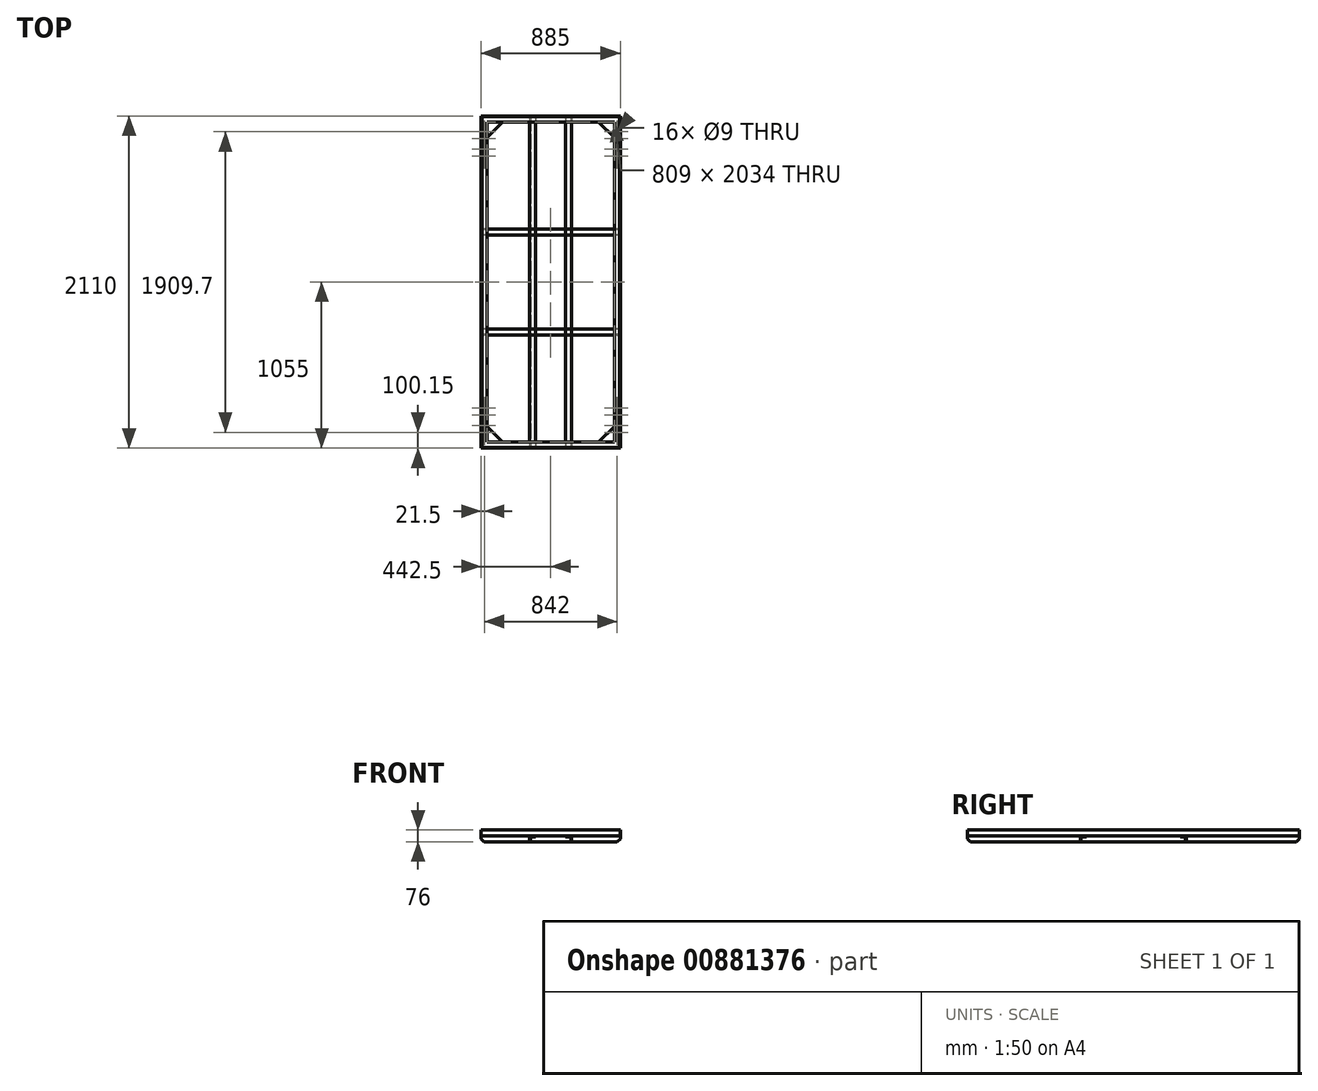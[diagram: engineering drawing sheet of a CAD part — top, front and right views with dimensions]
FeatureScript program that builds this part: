
annotation { "Feature Type Name" : "Feature", "Feature Type Description" : "" }
export const myFeature = defineFeature(function(context is Context, id is Id, definition is map)
    precondition{}
    {
        {
            var Q0;
            Q0=qCreatedBy(makeId("Top.planeOp"),FACE);
            var sketch = newSketch(context, id + "F0", { "sketchPlane" : qUnion([Q0])});
            skLineSegment(sketch, "E0.bottom", {"start": v(0, 0) * mm, "end": v(875, 0) * mm});
            skLineSegment(sketch, "E0.top", {"start": v(0, 2100) * mm, "end": v(875, 2100) * mm});
            skLineSegment(sketch, "E0.left", {"start": v(0, 0) * mm, "end": v(0, 2100) * mm});
            skLineSegment(sketch, "E0.right", {"start": v(875, 0) * mm, "end": v(875, 2100) * mm});
            skSolve(sketch);
        }
        {
            var Q0;
            Q0=qCreatedBy(makeId("Front.planeOp"),FACE);
            var sketch = newSketch(context, id + "F1", { "sketchPlane" : qUnion([Q0])});
            skLineSegment(sketch, "E1", {"start": v(0, 0) * mm, "end": v(0, 33) * mm});
            skLineSegment(sketch, "E2", {"start": v(0, 33) * mm, "end": v(-5, 33) * mm});
            skLineSegment(sketch, "E3", {"start": v(-5, 33) * mm, "end": v(-5, -5) * mm});
            skLineSegment(sketch, "E4", {"start": v(-5, -5) * mm, "end": v(33, -5) * mm});
            skLineSegment(sketch, "E5", {"start": v(33, -5) * mm, "end": v(33, 0) * mm});
            skLineSegment(sketch, "E6", {"start": v(33, 0) * mm, "end": v(0, 0) * mm});
            skSolve(sketch);
        }
        {
            var Q0;
            Q0 = qSketchRegion(id + "F1", true);
            var Q1;
            Q1 = qConstructionFilter(qBodyType(qCreatedBy(id + "F0" ,EDGE), BodyType.WIRE), ConstructionObject.NO);
            sweep(context, id + "F2", {"profiles" : qUnion([Q0]), "path" : qUnion([Q1])});
        }
        {
            var Q0;
            Q0=makeQuery(id+"F2.opSweep","SWEPT_FACE",FACE,{"disambiguationData":[OSD([sQuery(id+"F0.wireOp",EDGE,"E0.left"),sQuery(id+"F1.wireOp",EDGE,"E3")])]});
            var sketch = newSketch(context, id + "F3", { "sketchPlane" : qUnion([Q0])});
            skLineSegment(sketch, "E7", {"start": v(-1387, -5) * mm, "end": v(-1387, -43) * mm});
            skLineSegment(sketch, "E8", {"start": v(-1387, -43) * mm, "end": v(-1382, -43) * mm});
            skLineSegment(sketch, "E9", {"start": v(-1382, -43) * mm, "end": v(-1382, -10) * mm});
            skLineSegment(sketch, "E10", {"start": v(-1382, -10) * mm, "end": v(-1349, -10) * mm});
            skLineSegment(sketch, "E11", {"start": v(-1349, -10) * mm, "end": v(-1349, -5) * mm});
            skLineSegment(sketch, "E12", {"start": v(-1349, -5) * mm, "end": v(-1387, -5) * mm});
            skLineSegment(sketch, "E13", {"start": v(-751, -5) * mm, "end": v(-713, -5) * mm});
            skLineSegment(sketch, "E14", {"start": v(-713, -5) * mm, "end": v(-713, -43) * mm});
            skLineSegment(sketch, "E15", {"start": v(-713, -43) * mm, "end": v(-718, -43) * mm});
            skLineSegment(sketch, "E16", {"start": v(-718, -43) * mm, "end": v(-718, -10) * mm});
            skLineSegment(sketch, "E17", {"start": v(-718, -10) * mm, "end": v(-751, -10) * mm});
            skLineSegment(sketch, "E18", {"start": v(-751, -10) * mm, "end": v(-751, -5) * mm});
            skLineSegment(sketch, "E19", {"start": v(-1050, 372.8) * mm, "end": v(-1050, -327.2) * mm, "construction": true});
            skSolve(sketch);
        }
        {
            var Q0;
            Q0 = qSketchRegion(id + "F3", true);
            var Q1;
            Q1=makeQuery(id+"F2.opSweep","SWEPT_FACE",FACE,{"disambiguationData":[OSD([sQuery(id+"F0.wireOp",EDGE,"E0.right"),sQuery(id+"F1.wireOp",EDGE,"E3")])]});
            extrude(context, id + "F4", {"entities" : qUnion([Q0]), "endBound" : BoundingType.UP_TO_SURFACE, "oppositeDirection" : true, "depth" : 25 * mm, "endBoundEntityFace" : qUnion([Q1]), "offsetDistance" : 25 * mm});
        }
        {
            var Q0;
            Q0=makeQuery(id+"F2.opSweep","SWEPT_FACE",FACE,{"disambiguationData":[OSD([sQuery(id+"F0.wireOp",EDGE,"E0.bottom"),sQuery(id+"F1.wireOp",EDGE,"E3")])]});
            var sketch = newSketch(context, id + "F5", { "sketchPlane" : qUnion([Q0])});
            skLineSegment(sketch, "E20", {"start": v(304, -43) * mm, "end": v(304, -5) * mm});
            skLineSegment(sketch, "E21", {"start": v(304, -5) * mm, "end": v(342, -5) * mm});
            skLineSegment(sketch, "E22", {"start": v(342, -5) * mm, "end": v(342, -10) * mm});
            skLineSegment(sketch, "E23", {"start": v(342, -10) * mm, "end": v(309, -10) * mm});
            skLineSegment(sketch, "E24", {"start": v(309, -10) * mm, "end": v(309, -43) * mm});
            skLineSegment(sketch, "E25", {"start": v(309, -43) * mm, "end": v(304, -43) * mm});
            skLineSegment(sketch, "E26", {"start": v(533, -5) * mm, "end": v(571, -5) * mm});
            skLineSegment(sketch, "E27", {"start": v(571, -5) * mm, "end": v(571, -43) * mm});
            skLineSegment(sketch, "E28", {"start": v(571, -43) * mm, "end": v(566, -43) * mm});
            skLineSegment(sketch, "E29", {"start": v(566, -43) * mm, "end": v(566, -10) * mm});
            skLineSegment(sketch, "E30", {"start": v(566, -10) * mm, "end": v(533, -10) * mm});
            skLineSegment(sketch, "E31", {"start": v(533, -10) * mm, "end": v(533, -5) * mm});
            skLineSegment(sketch, "E32", {"start": v(437.5, 33) * mm, "end": v(437.5, -45.66) * mm, "construction": true});
            skSolve(sketch);
        }
        {
            var Q0;
            Q0 = qSketchRegion(id + "F5", true);
            var Q1;
            Q1=makeQuery(id+"F2.opSweep","SWEPT_FACE",FACE,{"disambiguationData":[OSD([sQuery(id+"F0.wireOp",EDGE,"E0.top"),sQuery(id+"F1.wireOp",EDGE,"E3")])]});
            extrude(context, id + "F6", {"entities" : qUnion([Q0]), "endBound" : BoundingType.UP_TO_SURFACE, "oppositeDirection" : true, "depth" : 25 * mm, "endBoundEntityFace" : qUnion([Q1]), "offsetDistance" : 25 * mm});
        }
        {
            var Q0;
            Q0=makeQuery(id+"F2.opSweep","SWEPT_FACE",FACE,{"disambiguationData":[OSD([sQuery(id+"F0.wireOp",EDGE,"E0.left"),sQuery(id+"F1.wireOp",EDGE,"E4")])]});
            var sketch = newSketch(context, id + "F7", { "sketchPlane" : qUnion([Q0])});
            skLineSegment(sketch, "E33.bottom", {"start": v(845.8, -65) * mm, "end": v(871.2, -65) * mm});
            skLineSegment(sketch, "E33.top", {"start": v(845.8, -280.9) * mm, "end": v(871.2, -280.9) * mm});
            skLineSegment(sketch, "E33.left", {"start": v(845.8, -65) * mm, "end": v(845.8, -280.9) * mm});
            skLineSegment(sketch, "E33.right", {"start": v(871.2, -65) * mm, "end": v(871.2, -280.9) * mm});
            skLineSegment(sketch, "E34", {"start": v(858.5, 5) * mm, "end": v(858.5, -2105) * mm, "construction": true});
            skLineSegment(sketch, "E35", {"start": v(-5, -16.5) * mm, "end": v(880, -16.5) * mm, "construction": true});
            skPoint(sketch, "E36", {"position": v(858.5, -95.15) * mm});
            skPoint(sketch, "E37", {"position": v(858.5, -139.65) * mm});
            skPoint(sketch, "E38", {"position": v(858.5, -206.25) * mm});
            skPoint(sketch, "E39", {"position": v(858.5, -250.75) * mm});
            skLineSegment(sketch, "E40", {"start": v(871.2, -172.95) * mm, "end": v(845.8, -172.95) * mm, "construction": true});
            skLineSegment(sketch, "E41", {"start": v(437.5, 5) * mm, "end": v(437.5, -2105) * mm, "construction": true});
            skLineSegment(sketch, "E42", {"start": v(-5, -1050) * mm, "end": v(880, -1050) * mm, "construction": true});
            skPoint(sketch, "E43.MirrorP", {"position": v(16.5, -95.15) * mm});
            skPoint(sketch, "E44.MirrorP", {"position": v(16.5, -139.65) * mm});
            skPoint(sketch, "E45.MirrorP", {"position": v(16.5, -206.25) * mm});
            skPoint(sketch, "E46.MirrorP", {"position": v(16.5, -250.75) * mm});
            skPoint(sketch, "E47.MirrorP", {"position": v(16.5, -2004.85) * mm});
            skPoint(sketch, "E48.MirrorP", {"position": v(16.5, -1960.35) * mm});
            skPoint(sketch, "E49.MirrorP", {"position": v(16.5, -1893.75) * mm});
            skPoint(sketch, "E50.MirrorP", {"position": v(16.5, -1849.25) * mm});
            skPoint(sketch, "E51.MirrorP", {"position": v(858.5, -2004.85) * mm});
            skPoint(sketch, "E52.MirrorP", {"position": v(858.5, -1960.35) * mm});
            skPoint(sketch, "E53.MirrorP", {"position": v(858.5, -1893.75) * mm});
            skPoint(sketch, "E54.MirrorP", {"position": v(858.5, -1849.25) * mm});
            skSolve(sketch);
        }
        {
            var Q0;
            Q0=makeQuery(id+"F7.imprint","IMPRINT",FACE,{"disambiguationData":[TD([[makeQuery(id+"F7.imprint","IMPRINT",EDGE,{"derivedFrom":sQuery(id+"F7.wireOp",EDGE,"E33.bottom")}),1.0]])]});
            var sketch = newSketch(context, id + "F8", { "sketchPlane" : qUnion([Q0])});
            skLineSegment(sketch, "E55", {"start": v(33, -133) * mm, "end": v(133, -33) * mm});
            skLineSegment(sketch, "E56", {"start": v(133, -33) * mm, "end": v(33, -33) * mm});
            skLineSegment(sketch, "E57", {"start": v(33, -33) * mm, "end": v(33, -133) * mm});
            skLineSegment(sketch, "E58.MirrorCS", {"start": v(842, -133) * mm, "end": v(742, -33) * mm});
            skLineSegment(sketch, "E59.MirrorCS", {"start": v(842, -33) * mm, "end": v(842, -133) * mm});
            skLineSegment(sketch, "E60.MirrorCS", {"start": v(742, -33) * mm, "end": v(842, -33) * mm});
            skLineSegment(sketch, "E61.MirrorCS", {"start": v(133, -2067) * mm, "end": v(33, -2067) * mm});
            skLineSegment(sketch, "E62.MirrorCS", {"start": v(33, -1967) * mm, "end": v(133, -2067) * mm});
            skLineSegment(sketch, "E63.MirrorCS", {"start": v(33, -2067) * mm, "end": v(33, -1967) * mm});
            skLineSegment(sketch, "E64.MirrorCS", {"start": v(842, -1967) * mm, "end": v(742, -2067) * mm});
            skLineSegment(sketch, "E65.MirrorCS", {"start": v(742, -2067) * mm, "end": v(842, -2067) * mm});
            skLineSegment(sketch, "E66.MirrorCS", {"start": v(842, -2067) * mm, "end": v(842, -1967) * mm});
            skSolve(sketch);
        }
        {
            var Q0;
            Q0 = qSketchRegion(id + "F8", true);
            var Q1;
            Q1=makeQuery(id+"F2.opSweep","SWEPT_FACE",FACE,{"disambiguationData":[OSD([sQuery(id+"F0.wireOp",EDGE,"E0.left"),sQuery(id+"F1.wireOp",EDGE,"E6")])]});
            extrude(context, id + "F9", {"entities" : qUnion([Q0]), "endBound" : BoundingType.UP_TO_SURFACE, "oppositeDirection" : true, "depth" : 25 * mm, "endBoundEntityFace" : qUnion([Q1]), "offsetDistance" : 25 * mm});
        }
        {
            var Q0;
            Q0=makeQuery(id+"F2.opSweep","SWEPT_FACE",FACE,{"disambiguationData":[OSD([sQuery(id+"F0.wireOp",EDGE,"E0.left"),sQuery(id+"F1.wireOp",EDGE,"E6")])]});
            var sketch = newSketch(context, id + "F10", { "sketchPlane" : qUnion([Q0])});
            skPoint(sketch, "E67.0", {"position": v(858.5, 2004.85) * mm});
            skPoint(sketch, "E67.1", {"position": v(858.5, 1960.35) * mm});
            skPoint(sketch, "E67.2", {"position": v(858.5, 1893.75) * mm});
            skPoint(sketch, "E67.3", {"position": v(858.5, 1849.25) * mm});
            skPoint(sketch, "E67.4", {"position": v(858.5, 250.75) * mm});
            skPoint(sketch, "E67.5", {"position": v(858.5, 206.25) * mm});
            skPoint(sketch, "E67.6", {"position": v(858.5, 139.65) * mm});
            skPoint(sketch, "E67.7", {"position": v(858.5, 95.15) * mm});
            skPoint(sketch, "E67.8", {"position": v(16.5, 250.75) * mm});
            skPoint(sketch, "E67.9", {"position": v(16.5, 206.25) * mm});
            skPoint(sketch, "E67.10", {"position": v(16.5, 139.65) * mm});
            skPoint(sketch, "E67.11", {"position": v(16.5, 95.15) * mm});
            skPoint(sketch, "E67.12", {"position": v(16.5, 2004.85) * mm});
            skPoint(sketch, "E67.13", {"position": v(16.5, 1960.35) * mm});
            skPoint(sketch, "E67.14", {"position": v(16.5, 1893.75) * mm});
            skPoint(sketch, "E67.15", {"position": v(16.5, 1849.25) * mm});
            skSolve(sketch);
        }
        {
            var Q0;
            Q0=sQuery(id+"F10.wireOp",VERTEX,"E67.0");
            var Q1;
            Q1=sQuery(id+"F10.wireOp",VERTEX,"E67.1");
            var Q2;
            Q2=sQuery(id+"F10.wireOp",VERTEX,"E67.2");
            var Q3;
            Q3=sQuery(id+"F10.wireOp",VERTEX,"E67.3");
            var Q4;
            Q4=sQuery(id+"F10.wireOp",VERTEX,"E67.12");
            var Q5;
            Q5=sQuery(id+"F10.wireOp",VERTEX,"E67.13");
            var Q6;
            Q6=sQuery(id+"F10.wireOp",VERTEX,"E67.14");
            var Q7;
            Q7=sQuery(id+"F10.wireOp",VERTEX,"E67.15");
            var Q8;
            Q8=sQuery(id+"F10.wireOp",VERTEX,"E67.8");
            var Q9;
            Q9=sQuery(id+"F10.wireOp",VERTEX,"E67.9");
            var Q10;
            Q10=sQuery(id+"F10.wireOp",VERTEX,"E67.10");
            var Q11;
            Q11=sQuery(id+"F10.wireOp",VERTEX,"E67.11");
            var Q12;
            Q12=sQuery(id+"F10.wireOp",VERTEX,"E67.4");
            var Q13;
            Q13=sQuery(id+"F10.wireOp",VERTEX,"E67.5");
            var Q14;
            Q14=sQuery(id+"F10.wireOp",VERTEX,"E67.6");
            var Q15;
            Q15=sQuery(id+"F10.wireOp",VERTEX,"E67.7");
            var Q16;
            Q16=makeQuery(id+"F2.opSweep","SWEPT_BODY",BODY,{"disambiguationData":[OSD([sQuery(id+"F0.wireOp",EDGE,"E0.right"),sQuery(id+"F1.wireOp",EDGE,"E1"),sQuery(id+"F1.wireOp",EDGE,"E2"),sQuery(id+"F1.wireOp",EDGE,"E3"),sQuery(id+"F1.wireOp",EDGE,"E4"),sQuery(id+"F1.wireOp",EDGE,"E5"),sQuery(id+"F1.wireOp",EDGE,"E6")])]});
            hole(context, id + "F11", {"style" : HoleStyle.C_SINK, "endStyle" : HoleEndStyle.THROUGH, "standardTappedOrClearance" : lookupTablePath({ "fit" : "Normal", "standard" : "ISO", "size" : "M8", "type" : "Clearance" }), "standardBlindInLast" : lookupTablePath({ "fit" : "Normal", "standard" : "ISO", "size" : "M8", "type" : "Clearance" }), "holeDiameter" : 9 * mm, "cSinkDiameter" : 17.92 * mm, "cSinkAngle" : 90 * degree, "majorDiameter" : 5 * mm, "isTappedThrough" : true, "tappedDepth" : 12 * mm, "tapClearance" : 3, "locations" : qUnion([Q0, Q1, Q2, Q3, Q4, Q5, Q6, Q7, Q8, Q9, Q10, Q11, Q12, Q13, Q14, Q15]), "scope" : qUnion([Q16])});
        }
        {
            var Q0;
            Q0=makeQuery(id+"F4.opExtrude","CAP_EDGE",EDGE,{"disambiguationData":[OSD([sQuery(id+"F3.wireOp",EDGE,"E8")])],"isStart":false});
            var Q1;
            Q1=makeQuery(id+"F4.opExtrude","CAP_EDGE",EDGE,{"disambiguationData":[OSD([sQuery(id+"F3.wireOp",EDGE,"E8")])],"isStart":true});
            var Q2;
            Q2=makeQuery(id+"F6.opExtrude","CAP_EDGE",EDGE,{"disambiguationData":[OSD([sQuery(id+"F5.wireOp",EDGE,"E25")])],"isStart":false});
            var Q3;
            Q3=makeQuery(id+"F6.opExtrude","CAP_EDGE",EDGE,{"disambiguationData":[OSD([sQuery(id+"F5.wireOp",EDGE,"E28")])],"isStart":false});
            var Q4;
            Q4=makeQuery(id+"F4.opExtrude","CAP_EDGE",EDGE,{"disambiguationData":[OSD([sQuery(id+"F3.wireOp",EDGE,"E15")])],"isStart":true});
            var Q5;
            Q5=makeQuery(id+"F6.opExtrude","CAP_EDGE",EDGE,{"disambiguationData":[OSD([sQuery(id+"F5.wireOp",EDGE,"E25")])],"isStart":true});
            var Q6;
            Q6=makeQuery(id+"F6.opExtrude","CAP_EDGE",EDGE,{"disambiguationData":[OSD([sQuery(id+"F5.wireOp",EDGE,"E28")])],"isStart":true});
            var Q7;
            Q7=makeQuery(id+"F4.opExtrude","CAP_EDGE",EDGE,{"disambiguationData":[OSD([sQuery(id+"F3.wireOp",EDGE,"E15")])],"isStart":false});
            chamfer(context, id + "F12", {"entities" : qUnion([Q0, Q1, Q2, Q3, Q4, Q5, Q6, Q7]), "width" : 20 * mm, "tangentPropagation" : true});
        }
    });
